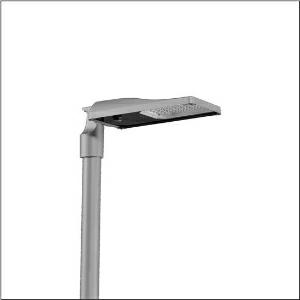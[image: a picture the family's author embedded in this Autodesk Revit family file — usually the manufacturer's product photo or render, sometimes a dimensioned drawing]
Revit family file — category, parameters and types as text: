
# Revit family: streetlight_sl_31_mini___st1_0a_5xh6d31r08ja_5198
name_source: partatom
category: Lighting Fixtures
units: mm (PartAtom-declared; Revit-internal decimal feet)

## family parameters
Cut with Voids When Loaded = No
Host = Face
Light Source = No
Part Type = Normal
Room Calculation Point = No
Round Connector Dimension = Use Diameter
Shared = No

## types (1)
- --- (1 x LED, 12270 lm, 82.5 W, 3000K)
    Apparent Load = 83 VA
    CIE Flux Codes = 40 73 97 100 100
    Color Rendering = 70
    Color Temperature = 3000K
    Default Elevation = 1800 mm
    Description = Streetlight SL 31 mini D4i, Desk-Remote mast luminaire for post-top, side-entry; light control with lens of PMMA; light distribution: ST1.0a, direct asymmetric distribution, for standard-compliant lighting for roads and squares; LED: luminous flux: 12.270lm, light colour: 730, colour temperature: 3000K; luminous efficacy: 148,7lm/W; control: pre-setting: logarithmic dimming characteristic, flexible luminous flux parameterisation, time-dependent luminous flux control, constant luminous flux control, power reduction, intelligent temperature release in ECG and LED module, overheat protection; luminaire housing, of diecast aluminium, SITECO metallic grey (DB 702S), corrosivity category C5 high according to DIN EN ISO 12944; cover of toughened safety glass, transparent, opened without tools; mast flange of diecast aluminium, SITECO metallic grey (DB 702S), spigot size: 76/60mm, mast flange included unmounted; with cable H07RN-F 2x 1.5mm², cable length: 10,5m, connection cable pre-assembled; mains connection: 220..240V, AC, 50/60Hz; power consumption (at start of service life): 82,5W / (at end of service life): 90,1W / (with reduced operation 50%): 36,8W; protection rating (complete): IP66; insulation class (complete): insulation class II (safety insulation); impact resistance: IK09; certification: CE, ENEC, ENEC+, VDE, UKCA, ZD4i; permissible operating ambient temperature for outdoor applications: -40..+50°C; packaging unit: 1 piece

Light Distribution: ST1.0a
    Height = 76 mm
    Lamp = 1 x LED
    Lamp Light Flux = 12270 lm
    Lamp Power = 82.5 W
    Lamp count = 1
    Length = 547 mm
    Luminous efficacy = 149 lm/W
    Manufacturer = Siteco
    ModVariant = No
    Model = 5XH6D31R08JA
    Number of Poles = 1
    OnlyDefault = Yes
    Power Factor = 1
    Product Name = Streetlight SL 31 mini | ST1.0a
    Product group = mast luminaire | pylon top
    ProductGroupID = 6100
    Protection Class = Protection class II
    Protection Degree = IP 66
    RLX_Detail_Level = 1
    RLX_Emergency_Light_Flux = 0 lm
    RLX_Emergency_Type = 0
    RLX_Emergency_Type_DB = No
    RlxData = <blob elided: 39817 chars, md5=49babd74>
    Socket = socket
    Standby Power = 0 W
    System Light Flux = 12270 lm
    System Power = 83 W
    Type Comments = factory setting: luminous flux: 100 % | dim-lin: 254 | 870 mA
    Type Image = l_1300328.jpg
    URL = http://relux.com
    VarID = @adj_057235
    Voltage = 0 V
    Weight = 0.00 kg
    Width = 265 mm

## geometry (parser evidence)
native form markers: Blend x4, Sweep x8
no freeform markers — native parametric forms only
